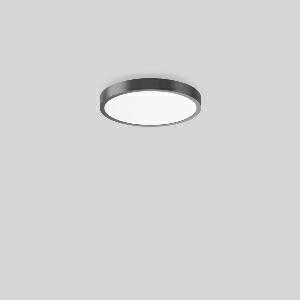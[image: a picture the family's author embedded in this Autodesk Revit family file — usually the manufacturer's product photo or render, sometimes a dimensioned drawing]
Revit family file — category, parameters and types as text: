
# Revit family: triona_round_a_312420_0031_2_730_85ab
name_source: partatom
category: Lighting Fixtures
units: mm (PartAtom-declared; Revit-internal decimal feet)

## family parameters
Cut with Voids When Loaded = No
Host = Face
Light Source = No
Part Type = Normal
Room Calculation Point = No
Round Connector Dimension = Use Diameter
Shared = No

## types (1)
- TuneableWhite 846 (1 x LED Modul 846, 3050 lm, 4600)
    Apparent Load = 38 VA
    CIE Flux Codes = 48 79 96 82 100
    Color Rendering = 80
    Color Temperature = 4600
    Default Elevation = 1800 mm
    Description = Series: TRIONA round
Decorative round LED surface-mounted luminaire. Flat, seamless frame: aluminium extrusion profile, powder coated. Cover made of sheet steel, powder-coated. Direct light emission through a diffuser plastic opal. Indirect light emission through a flush diffuser made of satin-finish plastic. Lightguide and diffuser made of non-yellowing plastic (PMMA). Lateral light emission (RZB SIDELITE technology) for above-average homogeneous light distribution. Direct 70%, indirect 30% light emission. Tunable white versions, dynamically adjustable from 2700 K to 6500 K. Suitable for Ceiling mounting, Wall (surface). Tool-free mounting via bayonet connection. Electronic ballast included. Very easy installation thanks to Plug+Play connection. With Casambi smart+free Bluetooth control for wireless network and operation using Android / iOS devices, free app available for download. Ideal for use as part of the Human Centric Lighting concept in connection with RZB light management systems. 
Colour: anthracite metallic (DB703)
Diameter: 461 mm
Height: 88 mm
Lamp: LED
Socket: without socket
Colour temperature: 2700K - 6500K
Colour rendering index (CRI): 80
System power: 38 W
Rated luminous flux: 3050 lm
Luminous efficiency: 80 lm/W
System power 2: 39 W
Rated luminous flux 2: 2900 lm
Luminous efficiency 2: 74 lm/W
System power 3: 39 W
Rated luminous flux 3: 2950 lm
Luminous efficiency 3: 76 lm/W
Control gear: Dimmable Bluetooth converter
Protection class: I
Type of protection: IP 20
    Height = 88 mm
    Lamp = 1 x LED Modul 846
    Lamp Light Flux = 3050 lm
    Lamp count = 1
    Length = 461 mm
    Lifetime = 50000 h
    Luminous efficacy = 80 lm/W
    Manufacturer = RZB
    ModVariant = No
    Model = 312420.0031.2.730
    Mounting Place = Ceiling
    Mounting Type = Surface mounted
    Number of Poles = 1
    OnlyDefault = Yes
    Power Factor = 1
    Product Name = TRIONA round A
    Product group = Surface mounted modular luminaires
    ProductGroupID = 306
    Protection Class = Protection class I
    Protection Degree = IP 20
    RLX_Detail_Level = 1
    RLX_Emergency_Light_Flux = 0 lm
    RLX_Emergency_Type = 0
    RLX_Emergency_Type_DB = No
    RlxData = <blob elided: 40213 chars, md5=6933a019>
    Socket = socket
    Standby Power = 0 W
    System Light Flux = 3050 lm
    System Power = 38 W
    Type Comments = TuneableWhite 846
    Type Image = 312420.0031.jpg
    URL = http://relux.com
    VarID = tuneablewhite_846
    Voltage = 230 V
    Voltage Range = 220-240 V
    Weight = 0.00 kg
    Width = 0 mm  [stored 0 ft]

note: [stored X ft] marks values corroborated as IEEE doubles in the binary element streams (Revit-internal decimal feet)

## geometry (parser evidence)
native form markers: Blend x4, Sweep x10
no freeform markers — native parametric forms only
